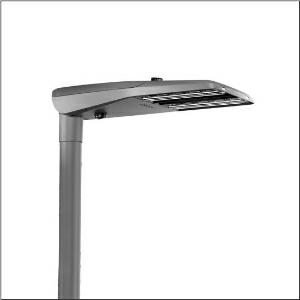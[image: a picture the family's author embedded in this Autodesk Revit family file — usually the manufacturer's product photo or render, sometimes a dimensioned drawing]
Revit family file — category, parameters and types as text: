
# Revit family: streetlight_sl_11_iq_midi___st1_2a_5xc3a51y08le_7352
name_source: partatom
category: Lighting Fixtures
units: mm (PartAtom-declared; Revit-internal decimal feet)

## family parameters
Cut with Voids When Loaded = No
Host = Face
Light Source = No
Part Type = Normal
Room Calculation Point = No
Round Connector Dimension = Use Diameter
Shared = No

## types (1)
- --- (1 x LED, 9210 lm, 59.4 W, 3000K)
    Apparent Load = 59 VA
    CIE Flux Codes = 32 70 96 100 100
    Color Rendering = 70
    Color Temperature = 3000K
    Default Elevation = 1800 mm
    Description = Streetlight SL 11 iQ midi, mast luminaire, primary light control with 3 zone facetted reflector, of plastic, silver coated, highly specular, primary optical cover: cover, of PMMA, transparent, light distribution: ST1.2a, light emission: direct distribution, primary light characteristic: asymmetric, installation type: post-top, side-entry, LED, High Power LED, rated luminous flux: 9.210lm, luminous efficacy: 156lm/W, light colour: 730, colour temperature: 3000K, control: presetting dimming logarithmic, Street-Remote, Auto-Match, Temp-Guard, Lumen-Switch, Night-Set, Smart-Wire, Light-Fading, Desk-Remote (wireless, voltage-free reading and setting of iQ features in the workshop via application-optimized NFC function/RFID function), optimised constant luminous flux control (CLO 2.0), with cable H07RN-F 5x 1.5mm², mains connection: 220..240V, AC, 50/60Hz, connection cable pre-assembled, cable length: 8,5m, start of lifetime: 59W, end of service life: 62W, reduction: 28W, luminaire housing, of diecast aluminium, powder-coated, Siteco® metallic grey (DB 702S), please order mast flange separately, inclination adjustable without tools: 0°, 5°, 10°, 15° (post-top) | 0°, -5°, -10°, -15° (side-entry), sealing non-destructively replaceable, multi-level sealing system, length: 780mm, width: 376mm, height: 118mm, spigot size: 60/76mm (post-top) and 42/60/76mm (side-entry), mast flange for spigot size: 42mm: 5XC10008XM4, 60mm: 5XC10008XM2, 76/60mm: 5XC10108XM1, equipment: standard, Smart Interface below and above, protection rating (complete): IP66, insulation class (complete): insulation class II (safety insulation), certification: CE, ENEC in preparation, impact resistance: IK09, permissible operating ambient temperature for outdoor applications: -25..+50°C, standard-compliant lighting for roads and squares, packaging unit: 1 piece

Light Distribution: ST1.2a
    Height = 118 mm
    Lamp = 1 x LED
    Lamp Light Flux = 9210 lm
    Lamp Power = 59.4 W
    Lamp count = 1
    Length = 780 mm
    Luminous efficacy = 155 lm/W
    Manufacturer = Siteco
    ModVariant = No
    Model = 5XC3A51Y08LE
    Number of Poles = 1
    OnlyDefault = Yes
    Power Factor = 1
    Product Name = Streetlight SL 11 iQ midi | ST1.2a
    Product group = mast luminaire | pylon top
    ProductGroupID = 6100
    Protection Class = Protection class II
    Protection Degree = IP 66
    RLX_Detail_Level = 1
    RlxData = <blob elided: 69649 chars, md5=3c780e40>
    Socket = socket
    Standby Power = 0 W
    System Light Flux = 9210 lm
    System Power = 59 W
    Type Comments = factory setting: luminous flux: 100 % | dim-lin: 254 | 521 mA
    Type Image = l_1004429.jpg
    URL = http://relux.com
    VarID = @adj_043733
    Voltage = 0 V
    Weight = 0.00 kg
    Width = 376 mm

## geometry (parser evidence)
native form markers: Blend x4, Sweep x10
no freeform markers — native parametric forms only
